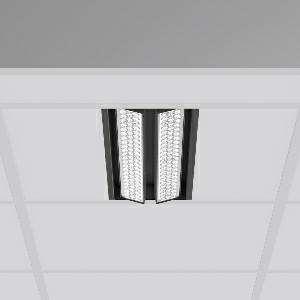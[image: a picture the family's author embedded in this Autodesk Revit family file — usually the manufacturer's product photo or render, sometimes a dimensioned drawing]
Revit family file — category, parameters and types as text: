
# Revit family: tx-move_901732_003_3_b3e6
name_source: partatom
category: Lighting Fixtures
units: mm (PartAtom-declared; Revit-internal decimal feet)

## family parameters
Cut with Voids When Loaded = No
Host = Face
Light Source = No
Part Type = Normal
Room Calculation Point = No
Round Connector Dimension = Use Diameter
Shared = No

## types (1)
- MultiLumen 1 (1 x LED Modul 835, 2775 lm, 3500)
    Apparent Load = 35 VA
    CIE Flux Codes = 88 96 99 100 100
    Color Rendering = 80
    Color Temperature = 3500
    Default Elevation = 1800 mm
    Description = Series: TX-MOVE
Einlege/Einbau-Flächenstrahler. Housing: sheet steel, powder-coated. 2xSwivel range: 90°. High-efficiency LED units with optimum light control thanks to clear plastic (PC) lens optics. Spezielle Mikrostrukturen reduzieren Gelbsaum. Symmetrical light distribution. Suitable for laying in grid ceiling module 600. Connected converter included in separate gearbox.Suitable for through-wiring.MultiLumen: Luminous flux adjustable in 3 steps. Accessories: Mounting frame for installation in suspended ceilings. Environmentally friendly and resource-saving due to replaceable and recyclable components. 
Colour: deep black, matt (RAL 9005)
Length: 597 mm
Width: 190 mm
Height: 39 mm
Cut-out length: 577.5 mm
Cut-out width: 174 mm
Recess height: 100 mm
Lamp: LED
Socket: without socket
Colour temperature: 3500K
Colour rendering index (CRI): 80
System power: 35 W
Rated luminous flux: 5550 lm
Luminous efficiency: 159 lm/W
System power 2: 47 W
Rated luminous flux 2: 7200 lm
Luminous efficiency 2: 153 lm/W
System power 3: 68 W
Rated luminous flux 3: 9900 lm
Luminous efficiency 3: 146 lm/W
Control gear: Regulated power supply
Protection class: I
Type of protection: IP 20
    Height = 0 mm  [stored 0 ft]
    Lamp = 1 x LED Modul 835
    Lamp Light Flux = 2775 lm
    Lamp count = 1
    Length = 597 mm
    Lifetime = 50000 h
    Luminous efficacy = 159 lm/W
    Manufacturer = RZB
    ModVariant = No
    Model = 901732.003.3
    Mounting Place = Ceiling, Wall
    Mounting Type = Recessed
    Number of Poles = 1
    OnlyDefault = Yes
    Power Factor = 1
    Product Name = TX-MOVE
    Product group = Recessed projectors
    ProductGroupID = 401
    Protection Class = Protection class I
    Protection Degree = IP 20
    RLX_Detail_Level = 1
    RLX_Emergency_Light_Flux = 0 lm
    RLX_Emergency_Type = 0
    RLX_Emergency_Type_DB = No
    RlxData = <blob elided: 37009 chars, md5=698fc4bb>
    Socket = socket
    Standby Power = 0 W
    System Light Flux = 5550 lm
    System Power = 35 W
    Type Comments = MultiLumen 1
    Type Image = 901733.003.jpg
    URL = http://relux.com
    VarID = multilumen_1
    Voltage = 230 V
    Voltage Range = 220-240 V
    Weight = 0.00 kg
    Width = 190 mm  [stored 0.62336 ft]

note: [stored X ft] marks values corroborated as IEEE doubles in the binary element streams (Revit-internal decimal feet)

## geometry (parser evidence)
native form markers: Blend x4, Sweep x14
no freeform markers — native parametric forms only
